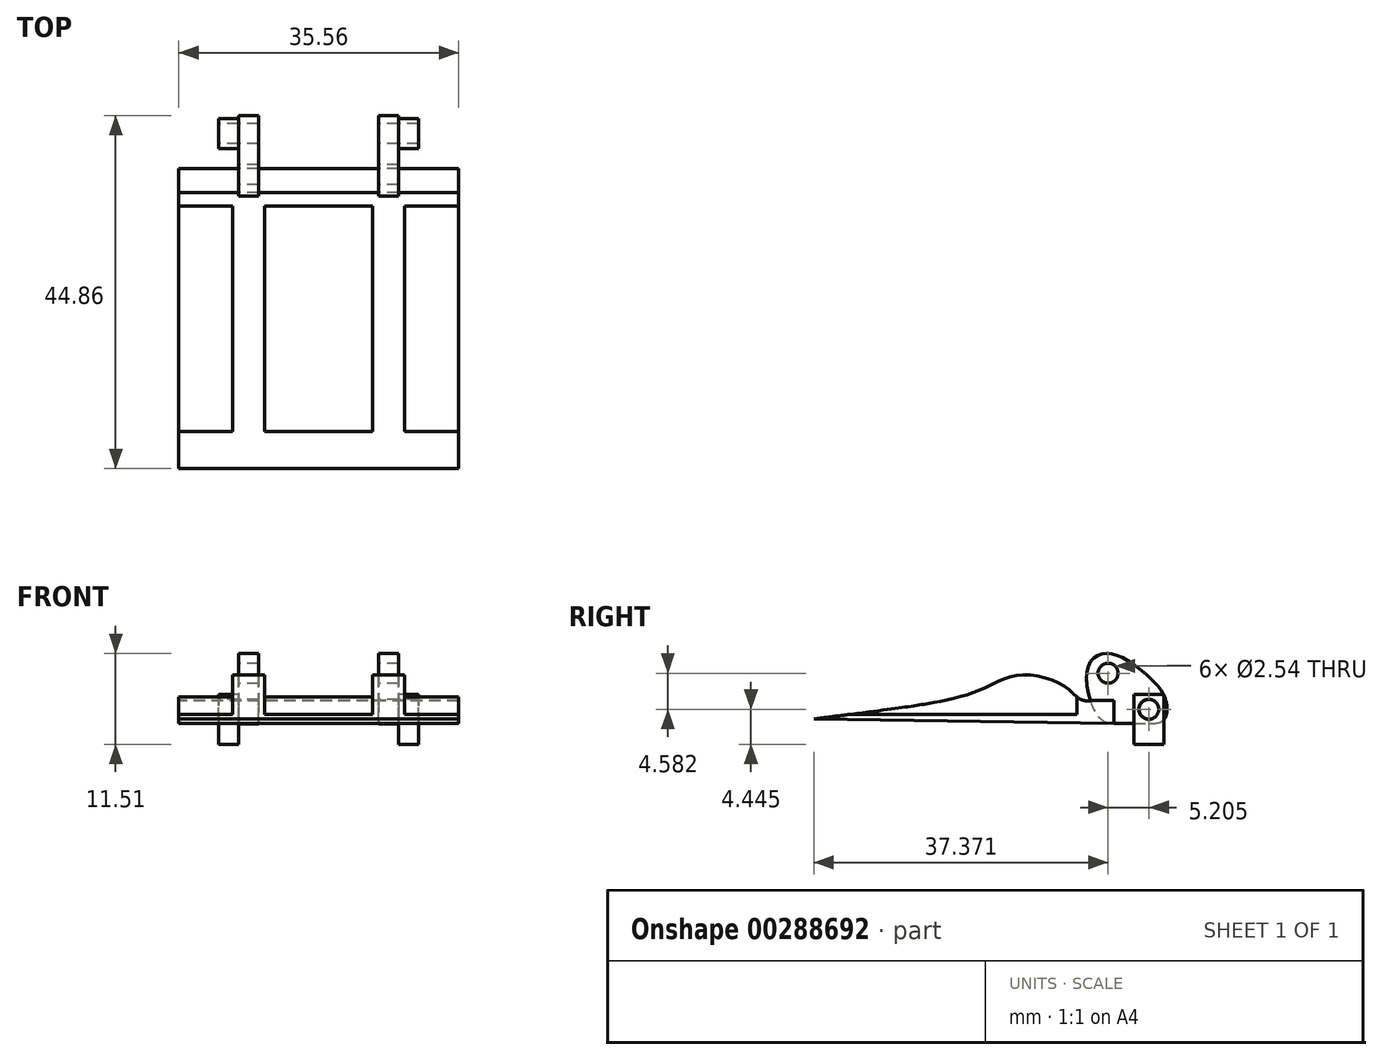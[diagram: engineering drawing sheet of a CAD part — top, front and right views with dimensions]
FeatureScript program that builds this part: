
annotation { "Feature Type Name" : "Feature", "Feature Type Description" : "" }
export const myFeature = defineFeature(function(context is Context, id is Id, definition is map)
    precondition{}
    {
        {
            var Q0;
            Q0=qCreatedBy(makeId("Top.planeOp"),FACE);
            var sketch = newSketch(context, id + "F0", { "sketchPlane" : qUnion([Q0])});
            skLineSegment(sketch, "E0.bottom", {"start": v(-50.8, 50.8) * mm, "end": v(50.8, 50.8) * mm});
            skLineSegment(sketch, "E0.top", {"start": v(-50.8, -50.8) * mm, "end": v(50.8, -50.8) * mm});
            skLineSegment(sketch, "E0.left", {"start": v(-50.8, 50.8) * mm, "end": v(-50.8, -50.8) * mm});
            skLineSegment(sketch, "E0.right", {"start": v(50.8, 50.8) * mm, "end": v(50.8, -50.8) * mm});
            skLineSegment(sketch, "E1", {"start": v(0, -50.8) * mm, "end": v(0, -20.32) * mm});
            skPoint(sketch, "E1.endSnap0", {"position": v(0, -50.8) * mm});
            skLineSegment(sketch, "E2", {"start": v(0, -20.32) * mm, "end": v(-22.86, -20.32) * mm});
            skLineSegment(sketch, "E3", {"start": v(0, -20.32) * mm, "end": v(22.86, -20.32) * mm});
            skLineSegment(sketch, "E4", {"start": v(22.86, -20.32) * mm, "end": v(22.86, -50.8) * mm});
            skLineSegment(sketch, "E5", {"start": v(-22.86, -20.32) * mm, "end": v(-22.86, -50.8) * mm});
            skLineSegment(sketch, "E6", {"start": v(-22.86, -50.8) * mm, "end": v(-22.86, -45.72) * mm});
            skLineSegment(sketch, "E7", {"start": v(-22.86, -45.72) * mm, "end": v(-20.32, -45.72) * mm});
            skLineSegment(sketch, "E8", {"start": v(-20.32, -45.72) * mm, "end": v(-20.32, -50.8) * mm});
            skLineSegment(sketch, "E9", {"start": v(20.32, -50.8) * mm, "end": v(20.32, -45.72) * mm});
            skLineSegment(sketch, "E10", {"start": v(20.32, -45.72) * mm, "end": v(22.86, -45.72) * mm});
            skSolve(sketch);
        }
        {
            var Q0;
            Q0=qCreatedBy(makeId("Right.planeOp"),FACE);
            var sketch = newSketch(context, id + "F1", { "sketchPlane" : qUnion([Q0])});
            skLineSegment(sketch, "E11", {"start": v(-49.14, 0) * mm, "end": v(-49.14, 6.35) * mm});
            skLineSegment(sketch, "E12", {"start": v(-49.14, 6.35) * mm, "end": v(-45.33, 6.35) * mm});
            skLineSegment(sketch, "E13", {"start": v(-45.33, 6.35) * mm, "end": v(-45.33, 0) * mm});
            skLineSegment(sketch, "E14", {"start": v(-3.42, 0) * mm, "end": v(-54.22, 0) * mm});
            skLineSegment(sketch, "E15", {"start": v(-54.22, 0) * mm, "end": v(-54.22, 15.24) * mm});
            skLineSegment(sketch, "E16", {"start": v(-54.26, 15.27) * mm, "end": v(-23.78, 15.27) * mm});
            skPoint(sketch, "E17.startSnap0", {"position": v(-47.24, 6.35) * mm});
            skLineSegment(sketch, "E18", {"start": v(-45.33, 2.54) * mm, "end": v(-49.14, 6.35) * mm});
            skLineSegment(sketch, "E19", {"start": v(-45.33, 6.35) * mm, "end": v(-49.14, 2.54) * mm});
            skPoint(sketch, "E17.start.orphan", {"position": v(-47.24, 0) * mm});
            skLineSegment(sketch, "E20", {"start": v(-45.33, 2.54) * mm, "end": v(-49.14, 2.54) * mm});
            skCircle(sketch, "E21", {"center": v(-47.24, 4.44) * mm, "radius": 1.27 * mm});
            skLineSegment(sketch, "E22", {"start": v(-3.42, 0) * mm, "end": v(-3.42, 16.88) * mm});
            skSolve(sketch);
        }
        {
            var Q0;
            Q0=qCreatedBy(makeId("Right.planeOp"),FACE);
            var sketch = newSketch(context, id + "F2", { "sketchPlane" : qUnion([Q0])});
            skFitSpline(sketch, "E23", {"points": [v(-50.54, 2.65) * mm, v(-47.45, 2.65) * mm, v(-45.36, 3.09) * mm, v(-45.1, 5.66) * mm, v(-47.63, 8.92) * mm, v(-52.09, 11.47) * mm, v(-54.89, 10) * mm, v(-53.52, 3.38) * mm, v(-50.54, 2.65) * mm]});
            skLineSegment(sketch, "E24", {"start": v(-54.68, 5.55) * mm, "end": v(-51.68, 5.55) * mm});
            skLineSegment(sketch, "E25", {"start": v(-51.68, 5.55) * mm, "end": v(-51.68, 2.62) * mm});
            skLineSegment(sketch, "E26", {"start": v(-51.68, 2.62) * mm, "end": v(-89.78, 3.2) * mm});
            skCircle(sketch, "E27", {"center": v(-52.4, 9.03) * mm, "radius": 1.27 * mm});
            skCircle(sketch, "E28", {"center": v(-47.2, 4.45) * mm, "radius": 1.27 * mm});
            skFitSpline(sketch, "E29", {"points": [v(-89.78, 3.2) * mm, v(-74.53, 5.3) * mm, v(-68.72, 6.88) * mm, v(-63.46, 8.8) * mm, v(-57.5, 7.04) * mm, v(-54.68, 5.55) * mm], "startDerivative": vector(99.95, 12.87) * mm, "endDerivative": vector(30.34, 4.77) * mm});
            skLineSegment(sketch, "E30", {"start": v(-74.53, 5.3) * mm, "end": v(-74.78, 2.98) * mm});
            skSolve(sketch);
        }
        {
            var Q0;
            Q0 = qSketchRegion(id + "F1", true);
            extrude(context, id + "F3", {"entities" : qUnion([Q0]), "depth" : 25.4 * mm, "symmetric" : true});
        }
        {
            var Q0;
            Q0 = qSketchRegion(id + "F1", true);
            extrude(context, id + "F4", {"entities" : qUnion([Q0]), "operationType" : NewBodyOperationType.REMOVE, "depth" : 20.32 * mm, "symmetric" : true});
        }
        {
            var Q0;
            {var subQ0=sQuery(id+"F2.wireOp",EDGE,"E24");Q0=makeQuery(id+"F2.imprint","IMPRINT",FACE,{"disambiguationData":[TD([[makeQuery(id+"F2.imprint","IMPRINT",EDGE,{"derivedFrom":subQ0}),-1.0]])]});}
            var Q1;
            {var subQ1=sQuery(id+"F2.wireOp",EDGE,"E24");Q1=makeQuery(id+"F2.imprint","IMPRINT",FACE,{"disambiguationData":[TD([[makeQuery(id+"F2.imprint","IMPRINT",EDGE,{"derivedFrom":subQ1}),1.0]])]});}
            extrude(context, id + "F5", {"entities" : qUnion([Q0, Q1]), "depth" : 20.32 * mm, "symmetric" : true});
        }
        {
            var Q0;
            {var subQ1=sQuery(id+"F2.wireOp",EDGE,"E24");Q0=makeQuery(id+"F2.imprint","IMPRINT",FACE,{"disambiguationData":[TD([[makeQuery(id+"F2.imprint","IMPRINT",EDGE,{"derivedFrom":subQ1}),1.0]])]});}
            var Q1;
            {var subQ0=sQuery(id+"F2.wireOp",EDGE,"E24");Q1=makeQuery(id+"F2.imprint","IMPRINT",FACE,{"disambiguationData":[TD([[makeQuery(id+"F2.imprint","IMPRINT",EDGE,{"derivedFrom":subQ0}),-1.0]])]});}
            extrude(context, id + "F6", {"entities" : qUnion([Q0, Q1]), "operationType" : NewBodyOperationType.REMOVE, "oppositeDirection" : true, "depth" : 15.24 * mm, "symmetric" : true});
        }
        {
            var Q0;
            {var subQ5=sQuery(id+"F2.wireOp",EDGE,"E30");Q0=makeQuery(id+"F2.imprint","IMPRINT",FACE,{"disambiguationData":[TD([[makeQuery(id+"F2.imprint","IMPRINT",EDGE,{"derivedFrom":subQ5}),1.0]])]});}
            var Q1;
            {var subQ3=sQuery(id+"F2.wireOp",EDGE,"E30");Q1=makeQuery(id+"F2.imprint","IMPRINT",FACE,{"disambiguationData":[TD([[makeQuery(id+"F2.imprint","IMPRINT",EDGE,{"derivedFrom":subQ3}),-1.0]])]});}
            var Q2;
            {var subQ0=sQuery(id+"F2.wireOp",EDGE,"E24");Q2=makeQuery(id+"F2.imprint","IMPRINT",FACE,{"disambiguationData":[TD([[makeQuery(id+"F2.imprint","IMPRINT",EDGE,{"derivedFrom":subQ0}),-1.0]])]});}
            extrude(context, id + "F7", {"entities" : qUnion([Q0, Q1, Q2]), "depth" : 35.56 * mm, "symmetric" : true});
        }
        {
            var Q0;
            Q0=qCreatedBy(makeId("Top.planeOp"),FACE);
            var sketch = newSketch(context, id + "F8", { "sketchPlane" : qUnion([Q0])});
            skLineSegment(sketch, "E31", {"start": v(0, -51.69) * mm, "end": v(17.78, -51.69) * mm});
            skLineSegment(sketch, "E32", {"start": v(17.78, -51.69) * mm, "end": v(17.78, -89.79) * mm});
            skLineSegment(sketch, "E33", {"start": v(17.78, -89.79) * mm, "end": v(-17.78, -89.79) * mm});
            skLineSegment(sketch, "E34", {"start": v(-17.78, -89.79) * mm, "end": v(-17.78, -51.69) * mm});
            skLineSegment(sketch, "E35", {"start": v(-17.78, -51.69) * mm, "end": v(0, -51.69) * mm});
            skLineSegment(sketch, "E36", {"start": v(0, -51.69) * mm, "end": v(0, -89.79) * mm});
            skLineSegment(sketch, "E37", {"start": v(17.78, -51.69) * mm, "end": v(0, -89.79) * mm});
            skLineSegment(sketch, "E38", {"start": v(-17.81, -51.81) * mm, "end": v(0, -89.79) * mm});
            skLineSegment(sketch, "E39", {"start": v(-17.78, -89.79) * mm, "end": v(0, -51.69) * mm});
            skLineSegment(sketch, "E40", {"start": v(17.78, -89.79) * mm, "end": v(0, -51.69) * mm});
            skLineSegment(sketch, "E41", {"start": v(8.89, -70.74) * mm, "end": v(8.89, -89.79) * mm});
            skLineSegment(sketch, "E42", {"start": v(-8.9, -70.74) * mm, "end": v(-8.9, -89.79) * mm});
            skLineSegment(sketch, "E43", {"start": v(-17.78, -64.39) * mm, "end": v(17.78, -64.39) * mm});
            skLineSegment(sketch, "E44", {"start": v(-8.89, -82.3) * mm, "end": v(-6.86, -82.3) * mm});
            skLineSegment(sketch, "E45", {"start": v(-6.86, -82.3) * mm, "end": v(-8.89, -82.3) * mm});
            skLineSegment(sketch, "E46", {"start": v(-10.92, -82.3) * mm, "end": v(-8.89, -82.3) * mm});
            skLineSegment(sketch, "E47", {"start": v(-6.86, -82.3) * mm, "end": v(-6.86, -51.69) * mm});
            skLineSegment(sketch, "E48", {"start": v(-10.92, -82.3) * mm, "end": v(-10.92, -51.69) * mm});
            skLineSegment(sketch, "E49", {"start": v(-6.86, -82.3) * mm, "end": v(-6.86, -89.79) * mm});
            skLineSegment(sketch, "E50", {"start": v(-10.92, -82.3) * mm, "end": v(-10.92, -89.79) * mm});
            skLineSegment(sketch, "E51", {"start": v(8.89, -81.4) * mm, "end": v(10.92, -81.4) * mm});
            skLineSegment(sketch, "E52", {"start": v(8.89, -81.4) * mm, "end": v(6.86, -81.4) * mm});
            skLineSegment(sketch, "E53", {"start": v(10.92, -81.4) * mm, "end": v(10.92, -89.79) * mm});
            skLineSegment(sketch, "E54", {"start": v(6.86, -81.4) * mm, "end": v(6.86, -89.79) * mm});
            skLineSegment(sketch, "E55", {"start": v(10.92, -81.4) * mm, "end": v(10.92, -51.69) * mm});
            skLineSegment(sketch, "E56", {"start": v(6.86, -81.4) * mm, "end": v(6.86, -51.69) * mm});
            skPoint(sketch, "E56.endSnap0", {"position": v(8.89, -51.69) * mm});
            skLineSegment(sketch, "E57", {"start": v(-17.78, -56.4) * mm, "end": v(17.78, -56.4) * mm});
            skSolve(sketch);
        }
        {
            var Q0;
            {var subQ3=sQuery(id+"F8.wireOp",EDGE,"E50");Q0=makeQuery(id+"F8.imprint","IMPRINT",FACE,{"disambiguationData":[TD([[makeQuery(id+"F8.imprint","IMPRINT",EDGE,{"derivedFrom":subQ3}),-1.0]])]});}
            var Q1;
            {var subQ0=sQuery(id+"F8.wireOp",EDGE,"E43");var subQ3=sQuery(id+"F8.wireOp",EDGE,"E38");var subQ4=makeQuery(id+"F8.imprint","INTERSECT",VERTEX,{"derivedFrom":[subQ3,subQ0]});Q1=makeQuery(id+"F8.imprint","IMPRINT",FACE,{"disambiguationData":[TD([[makeQuery(id+"F8.imprint","IMPRINT",EDGE,{"disambiguationData":[TD([[subQ4,-1.0]])],"derivedFrom":subQ3}),-1.0]])]});}
            var Q2;
            {var subQ0=sQuery(id+"F8.wireOp",EDGE,"E43");var subQ1=sQuery(id+"F8.wireOp",EDGE,"E34");var subQ2=makeQuery(id+"F8.imprint","INTERSECT",VERTEX,{"derivedFrom":[subQ1,subQ0]});Q2=makeQuery(id+"F8.imprint","IMPRINT",FACE,{"disambiguationData":[TD([[makeQuery(id+"F8.imprint","IMPRINT",EDGE,{"disambiguationData":[TD([[subQ2,-1.0]])],"derivedFrom":subQ1}),-1.0]])]});}
            var Q3;
            {var subQ0=sQuery(id+"F8.wireOp",EDGE,"E57");var subQ1=sQuery(id+"F8.wireOp",EDGE,"E38");var subQ2=makeQuery(id+"F8.imprint","INTERSECT",VERTEX,{"derivedFrom":[subQ1,subQ0]});Q3=makeQuery(id+"F8.imprint","IMPRINT",FACE,{"disambiguationData":[TD([[makeQuery(id+"F8.imprint","IMPRINT",EDGE,{"disambiguationData":[TD([[subQ2,-1.0]])],"derivedFrom":subQ1}),1.0]])]});}
            var Q4;
            {var subQ0=sQuery(id+"F8.wireOp",EDGE,"E43");var subQ1=sQuery(id+"F8.wireOp",EDGE,"E39");var subQ2=makeQuery(id+"F8.imprint","INTERSECT",VERTEX,{"derivedFrom":[subQ1,subQ0]});Q4=makeQuery(id+"F8.imprint","IMPRINT",FACE,{"disambiguationData":[TD([[makeQuery(id+"F8.imprint","IMPRINT",EDGE,{"disambiguationData":[TD([[subQ2,-1.0]])],"derivedFrom":subQ1}),1.0]])]});}
            var Q5;
            {var subQ0=sQuery(id+"F8.wireOp",EDGE,"E57");var subQ1=sQuery(id+"F8.wireOp",EDGE,"E36");var subQ2=makeQuery(id+"F8.imprint","INTERSECT",VERTEX,{"derivedFrom":[subQ1,subQ0]});Q5=makeQuery(id+"F8.imprint","IMPRINT",FACE,{"disambiguationData":[TD([[makeQuery(id+"F8.imprint","IMPRINT",EDGE,{"disambiguationData":[TD([[subQ2,-1.0]])],"derivedFrom":subQ1}),-1.0]])]});}
            var Q6;
            {var subQ3=sQuery(id+"F8.wireOp",EDGE,"E39");var subQ5=sQuery(id+"F8.wireOp",EDGE,"E47");var subQ6=makeQuery(id+"F8.imprint","INTERSECT",VERTEX,{"derivedFrom":[subQ3,subQ5]});Q6=makeQuery(id+"F8.imprint","IMPRINT",FACE,{"disambiguationData":[TD([[makeQuery(id+"F8.imprint","IMPRINT",EDGE,{"disambiguationData":[TD([[subQ6,-1.0]])],"derivedFrom":subQ3}),-1.0]])]});}
            var Q7;
            {var subQ0=sQuery(id+"F8.wireOp",EDGE,"E47");var subQ1=sQuery(id+"F8.wireOp",EDGE,"E39");var subQ2=makeQuery(id+"F8.imprint","INTERSECT",VERTEX,{"derivedFrom":[subQ1,subQ0]});Q7=makeQuery(id+"F8.imprint","IMPRINT",FACE,{"disambiguationData":[TD([[makeQuery(id+"F8.imprint","IMPRINT",EDGE,{"disambiguationData":[TD([[subQ2,-1.0]])],"derivedFrom":subQ1}),1.0]])]});}
            var Q8;
            {var subQ0=sQuery(id+"F8.wireOp",EDGE,"E43");var subQ1=sQuery(id+"F8.wireOp",EDGE,"E38");var subQ2=makeQuery(id+"F8.imprint","INTERSECT",VERTEX,{"derivedFrom":[subQ1,subQ0]});Q8=makeQuery(id+"F8.imprint","IMPRINT",FACE,{"disambiguationData":[TD([[makeQuery(id+"F8.imprint","IMPRINT",EDGE,{"disambiguationData":[TD([[subQ2,-1.0]])],"derivedFrom":subQ1}),1.0]])]});}
            var Q9;
            {var subQ3=sQuery(id+"F8.wireOp",EDGE,"E49");Q9=makeQuery(id+"F8.imprint","IMPRINT",FACE,{"disambiguationData":[TD([[makeQuery(id+"F8.imprint","IMPRINT",EDGE,{"derivedFrom":subQ3}),1.0]])]});}
            var Q10;
            {var subQ3=sQuery(id+"F8.wireOp",EDGE,"E54");Q10=makeQuery(id+"F8.imprint","IMPRINT",FACE,{"disambiguationData":[TD([[makeQuery(id+"F8.imprint","IMPRINT",EDGE,{"derivedFrom":subQ3}),-1.0]])]});}
            var Q11;
            {var subQ3=sQuery(id+"F8.wireOp",EDGE,"E40");var subQ5=sQuery(id+"F8.wireOp",EDGE,"E56");var subQ6=makeQuery(id+"F8.imprint","INTERSECT",VERTEX,{"derivedFrom":[subQ3,subQ5]});Q11=makeQuery(id+"F8.imprint","IMPRINT",FACE,{"disambiguationData":[TD([[makeQuery(id+"F8.imprint","IMPRINT",EDGE,{"disambiguationData":[TD([[subQ6,-1.0]])],"derivedFrom":subQ3}),1.0]])]});}
            var Q12;
            {var subQ0=sQuery(id+"F8.wireOp",EDGE,"E57");var subQ1=sQuery(id+"F8.wireOp",EDGE,"E36");var subQ2=makeQuery(id+"F8.imprint","INTERSECT",VERTEX,{"derivedFrom":[subQ1,subQ0]});Q12=makeQuery(id+"F8.imprint","IMPRINT",FACE,{"disambiguationData":[TD([[makeQuery(id+"F8.imprint","IMPRINT",EDGE,{"disambiguationData":[TD([[subQ2,-1.0]])],"derivedFrom":subQ1}),1.0]])]});}
            var Q13;
            {var subQ0=sQuery(id+"F8.wireOp",EDGE,"E43");var subQ1=sQuery(id+"F8.wireOp",EDGE,"E40");var subQ2=makeQuery(id+"F8.imprint","INTERSECT",VERTEX,{"derivedFrom":[subQ1,subQ0]});Q13=makeQuery(id+"F8.imprint","IMPRINT",FACE,{"disambiguationData":[TD([[makeQuery(id+"F8.imprint","IMPRINT",EDGE,{"disambiguationData":[TD([[subQ2,-1.0]])],"derivedFrom":subQ1}),-1.0]])]});}
            var Q14;
            {var subQ0=sQuery(id+"F8.wireOp",EDGE,"E57");var subQ1=sQuery(id+"F8.wireOp",EDGE,"E37");var subQ2=makeQuery(id+"F8.imprint","INTERSECT",VERTEX,{"derivedFrom":[subQ1,subQ0]});Q14=makeQuery(id+"F8.imprint","IMPRINT",FACE,{"disambiguationData":[TD([[makeQuery(id+"F8.imprint","IMPRINT",EDGE,{"disambiguationData":[TD([[subQ2,-1.0]])],"derivedFrom":subQ1}),-1.0]])]});}
            var Q15;
            {var subQ0=sQuery(id+"F8.wireOp",EDGE,"E43");var subQ1=sQuery(id+"F8.wireOp",EDGE,"E32");var subQ2=makeQuery(id+"F8.imprint","INTERSECT",VERTEX,{"derivedFrom":[subQ1,subQ0]});Q15=makeQuery(id+"F8.imprint","IMPRINT",FACE,{"disambiguationData":[TD([[makeQuery(id+"F8.imprint","IMPRINT",EDGE,{"disambiguationData":[TD([[subQ2,1.0]])],"derivedFrom":subQ1}),-1.0]])]});}
            var Q16;
            {var subQ0=sQuery(id+"F8.wireOp",EDGE,"E43");var subQ3=sQuery(id+"F8.wireOp",EDGE,"E37");var subQ4=makeQuery(id+"F8.imprint","INTERSECT",VERTEX,{"derivedFrom":[subQ3,subQ0]});Q16=makeQuery(id+"F8.imprint","IMPRINT",FACE,{"disambiguationData":[TD([[makeQuery(id+"F8.imprint","IMPRINT",EDGE,{"disambiguationData":[TD([[subQ4,-1.0]])],"derivedFrom":subQ3}),1.0]])]});}
            var Q17;
            {var subQ3=sQuery(id+"F8.wireOp",EDGE,"E53");Q17=makeQuery(id+"F8.imprint","IMPRINT",FACE,{"disambiguationData":[TD([[makeQuery(id+"F8.imprint","IMPRINT",EDGE,{"derivedFrom":subQ3}),1.0]])]});}
            var Q18;
            {var subQ0=sQuery(id+"F8.wireOp",EDGE,"E43");var subQ1=sQuery(id+"F8.wireOp",EDGE,"E37");var subQ2=makeQuery(id+"F8.imprint","INTERSECT",VERTEX,{"derivedFrom":[subQ1,subQ0]});Q18=makeQuery(id+"F8.imprint","IMPRINT",FACE,{"disambiguationData":[TD([[makeQuery(id+"F8.imprint","IMPRINT",EDGE,{"disambiguationData":[TD([[subQ2,-1.0]])],"derivedFrom":subQ1}),-1.0]])]});}
            var Q19;
            {var subQ0=sQuery(id+"F8.wireOp",EDGE,"E56");var subQ1=sQuery(id+"F8.wireOp",EDGE,"E40");var subQ2=makeQuery(id+"F8.imprint","INTERSECT",VERTEX,{"derivedFrom":[subQ1,subQ0]});Q19=makeQuery(id+"F8.imprint","IMPRINT",FACE,{"disambiguationData":[TD([[makeQuery(id+"F8.imprint","IMPRINT",EDGE,{"disambiguationData":[TD([[subQ2,-1.0]])],"derivedFrom":subQ1}),-1.0]])]});}
            extrude(context, id + "F9", {"entities" : qUnion([Q0, Q1, Q2, Q3, Q4, Q5, Q6, Q7, Q8, Q9, Q10, Q11, Q12, Q13, Q14, Q15, Q16, Q17, Q18, Q19]), "operationType" : NewBodyOperationType.REMOVE, "depth" : 14.25 * mm, "hasSecondDirection" : true, "secondDirectionOppositeDirection" : false, "secondDirectionDepth" : 3.8 * mm});
        }
    });
